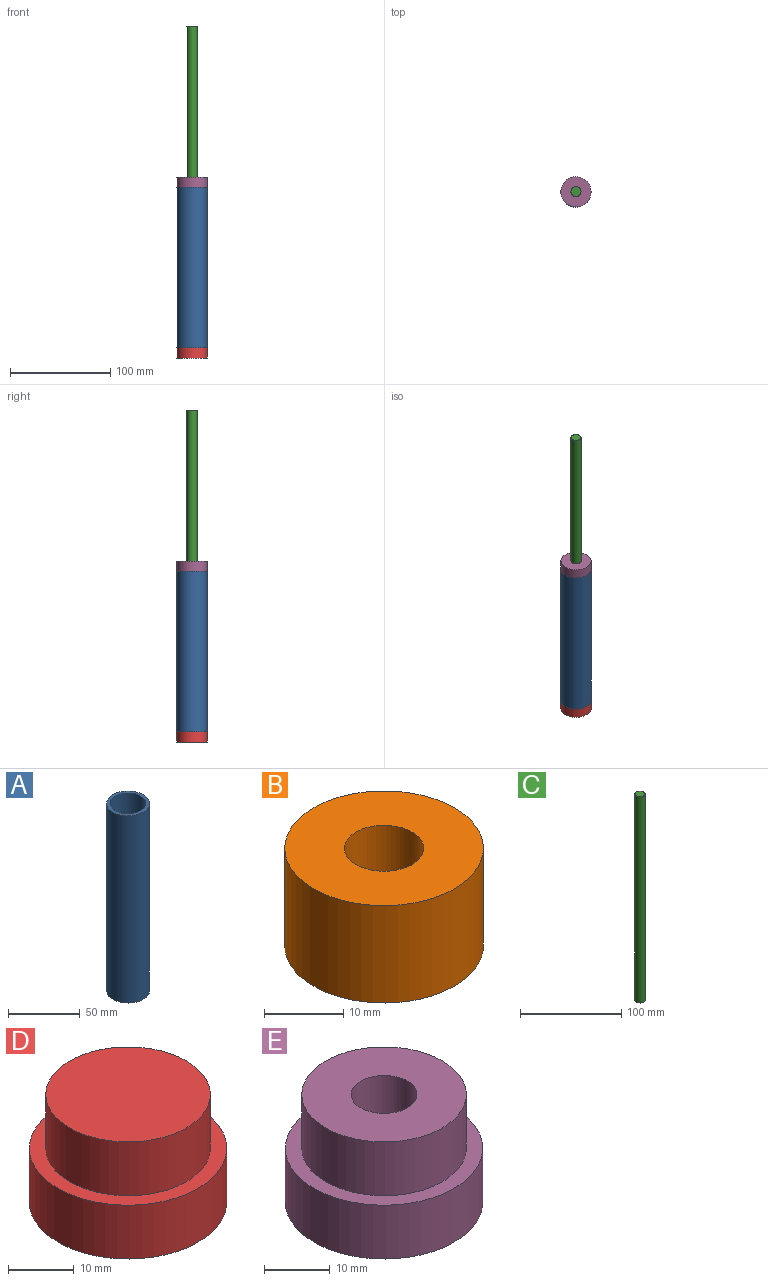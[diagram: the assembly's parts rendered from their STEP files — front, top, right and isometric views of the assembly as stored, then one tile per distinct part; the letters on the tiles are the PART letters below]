
ASSEMBLY  parts=5 mates=4
PART A: 4 faces, bbox 30x30x160 mm
  f0: cylinder r=12.5mm len=160mm, axis (0,0,-1), area 12566.4mm2, adj f2,f3
  f1: cylinder r=15mm len=160mm, axis (0,0,-1), area 15079.6mm2, adj f2,f3
  f2: plane 30x30mm, normal (0,0,1), area 216mm2, adj f0,f1
  f3: plane 30x30mm, normal (0,0,-1), area 216mm2, adj f0,f1
PART B: 4 faces, bbox 25x25x15 mm
  f0: cylinder r=5mm len=15mm, axis (0,0,-1), area 471.2mm2, adj f2,f3
  f1: cylinder r=12.5mm len=25mm, axis (0,0,-1), area 1178.1mm2, adj f2,f3
  f2: plane 25x25mm, normal (0,0,1), area 412.3mm2, adj f0,f1
  f3: plane 25x25mm, normal (0,0,-1), area 412.3mm2, adj f0,f1
PART C: 3 faces, bbox 10x10x250 mm
  f0: cylinder r=5mm len=250mm, axis (0,0,-1), area 7854mm2, adj f1,f2
  f1: plane 10x10mm, normal (0,0,1), area 78.5mm2, adj f0
  f2: plane 10x10mm, normal (0,0,-1), area 78.5mm2, adj f0
PART D: 5 faces, bbox 30x30x20 mm
  f0: cylinder r=15mm len=30mm, axis (0,0,-1), area 942.5mm2, adj f1,f2
  f1: plane 30x30mm, normal (0,0,1), area 216mm2, adj f0,f3
  f2: plane 30x30mm, normal (0,0,-1), area 706.9mm2, adj f0
  f3: cylinder r=12.5mm len=25mm, axis (0,0,-1), area 785.4mm2, adj f1,f4
  f4: plane 25x25mm, normal (0,0,1), area 490.9mm2, adj f3
PART E: 6 faces, bbox 30x30x20 mm
  f0: cylinder r=15mm len=30mm, axis (0,0,-1), area 942.5mm2, adj f1,f2
  f1: plane 30x30mm, normal (0,0,1), area 216mm2, adj f0,f3
  f2: plane 30x30mm, normal (0,0,-1), area 628.3mm2, adj f0,f5
  f3: cylinder r=12.5mm len=25mm, axis (0,0,-1), area 785.4mm2, adj f1,f4
  f4: plane 25x25mm, normal (0,0,1), area 412.3mm2, adj f3,f5
  f5: cylinder r=5mm len=20mm, axis (0,0,1), area 628.3mm2, adj f2,f4
PLACE A t=(-145.03,-57.63,-77.54)mm
PLACE B t=(-223.6,-4.51,-7.04)mm
PLACE C t=(-198.83,-20.46,-7.04)mm
PLACE D t=(-159.52,4.16,-87.54)mm
PLACE E rot(axis=(1,0,0),180deg) t=(-200.22,-71.64,92.46)mm
MATE fastened B.f0 <-> C.f0  axis (0,0,-1) through (-204.78,-20.63,-7.04)mm
MATE fastened E.f0 <-> A.f0  axis (0,0,1) through (-204.78,-20.63,82.46)mm
MATE fastened D.f0 <-> A.f0  axis (0,0,1) through (-204.78,-20.63,-77.54)mm
MATE cylindrical B.f0 <-> A.f0  axis (0,0,-1) through (-204.78,-20.63,0.46)mm
